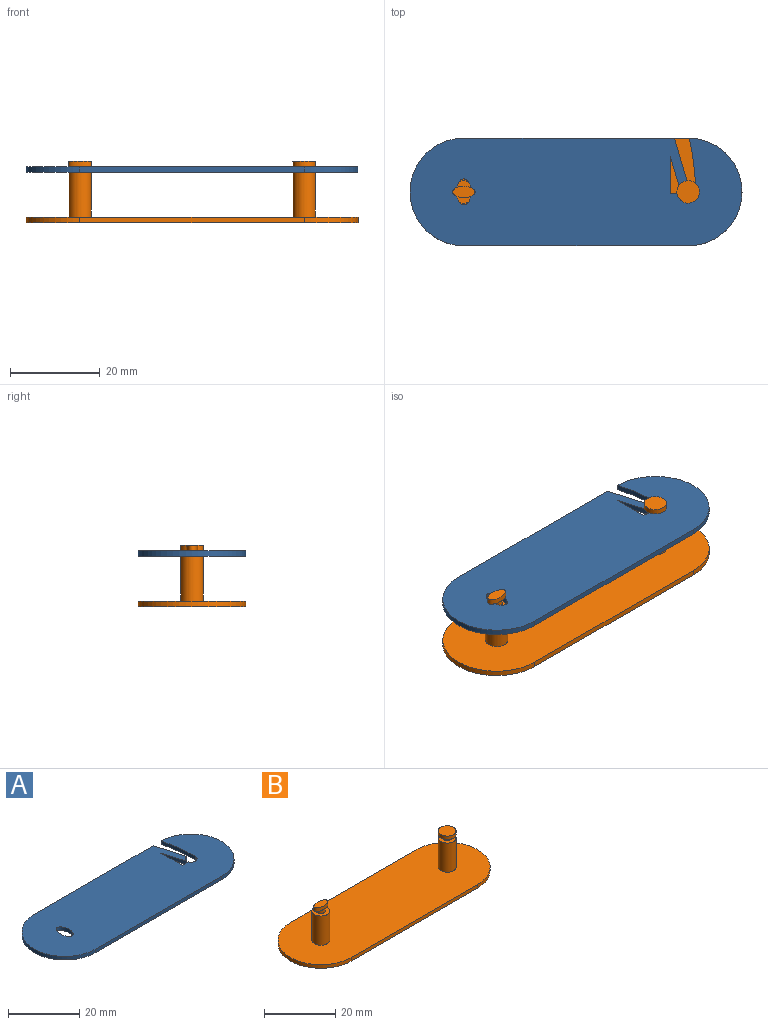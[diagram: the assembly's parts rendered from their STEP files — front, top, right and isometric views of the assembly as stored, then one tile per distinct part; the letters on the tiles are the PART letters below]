
ASSEMBLY  parts=2 mates=1
PART A: 14 faces, bbox 74x24x1.2 mm
  f0: cylinder r=12mm len=24mm, axis (0,0,-1), area 45.2mm2, adj f1,f11,f12,f13
  f1: plane 50x1.2mm, normal (0,-1,0), area 60mm2, adj f0,f2,f12,f13
  f2: cylinder r=12mm len=24mm, axis (0,0,-1), area 45mm2, adj f1,f3,f12,f13
  f3: cylinder r=51.65mm len=12mm, axis (0,0,-1), area 14.5mm2, adj f2,f4,f12,f13
  f4: cylinder r=1.65mm len=3.25mm, axis (0,0,-1), area 5.7mm2, adj f3,f5,f12,f13
  f5: plane 2.4x1.2mm, normal (0,1,0), area 2.9mm2, adj f4,f6,f12,f13
  f6: plane 8.34x1.2mm, normal (1,0,0), area 10mm2, adj f5,f7,f12,f13
  f7: plane 7.94x2.35mm, normal (-0.96,-0.28,0), area 9.9mm2, adj f6,f8,f12,f13
  f8: cylinder r=1.65mm len=1.65mm, axis (0,0,-1), area 3.1mm2, adj f7,f9,f12,f13
  f9: plane 10.35x3.06mm, normal (0.96,0.28,0), area 13mm2, adj f8,f11,f12,f13
  f10: extruded ~5.8x3.3mm, area 17.5mm2, adj f12,f13
  f11: plane 46.94x1.2mm, normal (0,1,0), area 56.3mm2, adj f0,f9,f12,f13
  f12: plane 74x24mm, normal (0,0,1), area 1590.6mm2, adj f0,f1,f2,f3,f4,f5,f6,f7
  f13: plane 74x24mm, normal (0,0,-1), area 1590.6mm2, adj f0,f1,f2,f3,f4,f5,f6,f7
PART B: 19 faces, bbox 74x24x13.6 mm
  f0: cylinder r=12mm len=24mm, axis (0,0,-1), area 45.2mm2, adj f1,f3,f4,f5
  f1: plane 50x1.2mm, normal (0,-1,0), area 60mm2, adj f0,f2,f4,f5
  f2: cylinder r=12mm len=24mm, axis (0,0,-1), area 45.2mm2, adj f1,f3,f4,f5
  f3: plane 50x1.2mm, normal (0,1,0), area 60mm2, adj f0,f2,f4,f5
  f4: plane 74x24mm, normal (0,0,1), area 1613.1mm2, adj f0,f1,f2,f3,f6,f8
  f5: plane 74x24mm, normal (0,0,-1), area 1652.4mm2, adj f0,f1,f2,f3
  f6: cylinder r=2.5mm len=10mm, axis (0,0,-1), area 157.1mm2, adj f4,f7
  f7: plane 5x5mm, normal (0,0,1), area 14.7mm2, adj f6,f10
  f8: cylinder r=2.5mm len=10mm, axis (0,0,-1), area 157.1mm2, adj f4,f9
  f9: plane 5x5mm, normal (0,0,1), area 14.7mm2, adj f8,f11
  f10: cylinder r=1.25mm len=2.5mm, axis (0,0,-1), area 9.4mm2, adj f7,f12,f15
  f11: cylinder r=1.25mm len=2.5mm, axis (0,0,-1), area 9.4mm2, adj f9,f18
  f12: plane 2.5x2.5mm, normal (0,0,-1), area 2.5mm2, adj f10,f13
  f13: extruded ~5x2.5mm, area 14.5mm2, adj f12,f14,f15
  f14: plane 5x2.5mm, normal (0,0,1), area 9.8mm2, adj f13
  f15: plane 2.5x2.5mm, normal (0,0,-1), area 2.5mm2, adj f10,f13
  f16: cylinder r=2.5mm len=5mm, axis (0,0,-1), area 18.8mm2, adj f17,f18
  f17: plane 5x5mm, normal (0,0,1), area 19.6mm2, adj f16
  f18: plane 5x5mm, normal (0,0,-1), area 14.7mm2, adj f11,f16
PLACE A rot(axis=(0,0,-1),0deg) t=(0,0,0)mm
PLACE B at identity fixed
MATE cylindrical A.f3 <-> B.f10  axis (0,0,1) through (0,0,12.4)mm
